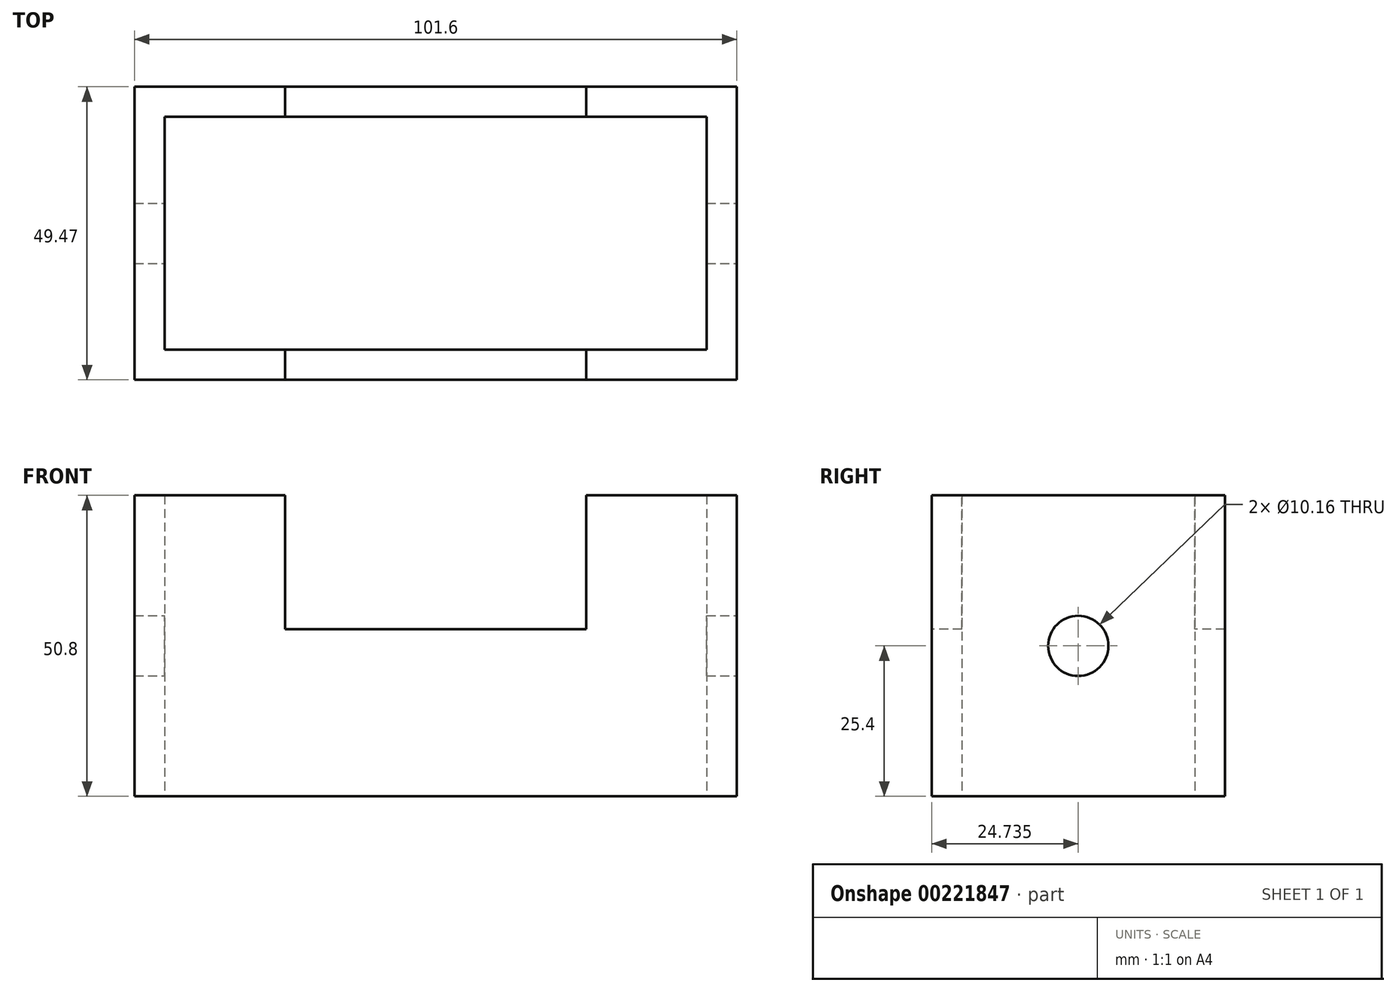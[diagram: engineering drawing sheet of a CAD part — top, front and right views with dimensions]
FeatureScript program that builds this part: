
annotation { "Feature Type Name" : "Feature", "Feature Type Description" : "" }
export const myFeature = defineFeature(function(context is Context, id is Id, definition is map)
    precondition{}
    {
        {
            var Q0;
            Q0=qCreatedBy(makeId("Top.planeOp"),FACE);
            var sketch = newSketch(context, id + "F0", { "sketchPlane" : qUnion([Q0])});
            skLineSegment(sketch, "E0.bottom", {"start": v(-45.7, 26.44) * mm, "end": v(55.9, 26.44) * mm});
            skLineSegment(sketch, "E0.top", {"start": v(-45.7, -23.03) * mm, "end": v(55.9, -23.03) * mm});
            skLineSegment(sketch, "E0.left", {"start": v(-45.7, 26.44) * mm, "end": v(-45.7, -23.03) * mm});
            skLineSegment(sketch, "E0.right", {"start": v(55.9, 26.44) * mm, "end": v(55.9, -23.03) * mm});
            skLineSegment(sketch, "E1.bottom", {"start": v(-40.63, 21.36) * mm, "end": v(50.81, 21.36) * mm});
            skLineSegment(sketch, "E1.top", {"start": v(-40.63, -17.95) * mm, "end": v(50.81, -17.95) * mm});
            skLineSegment(sketch, "E1.left", {"start": v(-40.63, 21.36) * mm, "end": v(-40.63, -17.95) * mm});
            skLineSegment(sketch, "E1.right", {"start": v(50.81, 21.36) * mm, "end": v(50.81, -17.95) * mm});
            skSolve(sketch);
        }
        {
            var Q0;
            Q0=makeQuery(id+"F0.imprint","IMPRINT",FACE,{"disambiguationData":[TD([[makeQuery(id+"F0.imprint","IMPRINT",EDGE,{"derivedFrom":sQuery(id+"F0.wireOp",EDGE,"E0.bottom")}),-1.0]])]});
            extrude(context, id + "F1", {"entities" : qUnion([Q0]), "depth" : 50.8 * mm});
        }
        {
            var Q0;
            Q0=makeQuery(id+"F1.opExtrude","SWEPT_FACE",FACE,{"disambiguationData":[OSD([sQuery(id+"F0.wireOp",EDGE,"E0.right")])]});
            var sketch = newSketch(context, id + "F2", { "sketchPlane" : qUnion([Q0])});
            skCircle(sketch, "E2", {"center": v(1.7, 25.4) * mm, "radius": 5.08 * mm});
            skPoint(sketch, "E2.centerSnap0", {"position": v(26.44, 25.4) * mm});
            skPoint(sketch, "E2.centerSnap1", {"position": v(1.7, 50.8) * mm});
            skSolve(sketch);
        }
        {
            var Q0;
            Q0 = qSketchRegion(id + "F2", true);
            extrude(context, id + "F3", {"entities" : qUnion([Q0]), "operationType" : NewBodyOperationType.REMOVE, "oppositeDirection" : true, "depth" : 114.3 * mm});
        }
        {
            var Q0;
            Q0=makeQuery(id+"F1.opExtrude","SWEPT_FACE",FACE,{"disambiguationData":[OSD([sQuery(id+"F0.wireOp",EDGE,"E0.top")])]});
            var sketch = newSketch(context, id + "F4", { "sketchPlane" : qUnion([Q0])});
            skLineSegment(sketch, "E3", {"start": v(-20.3, 50.8) * mm, "end": v(-20.3, 28.23) * mm});
            skLineSegment(sketch, "E4", {"start": v(-20.3, 28.23) * mm, "end": v(30.5, 28.23) * mm});
            skLineSegment(sketch, "E5", {"start": v(30.5, 28.23) * mm, "end": v(30.5, 50.8) * mm});
            skLineSegment(sketch, "E6", {"start": v(-20.3, 50.8) * mm, "end": v(30.5, 50.8) * mm});
            skSolve(sketch);
        }
        {
            var Q0;
            Q0 = qSketchRegion(id + "F4", true);
            extrude(context, id + "F5", {"entities" : qUnion([Q0]), "operationType" : NewBodyOperationType.REMOVE, "oppositeDirection" : true, "depth" : 63.5 * mm});
        }
    });
